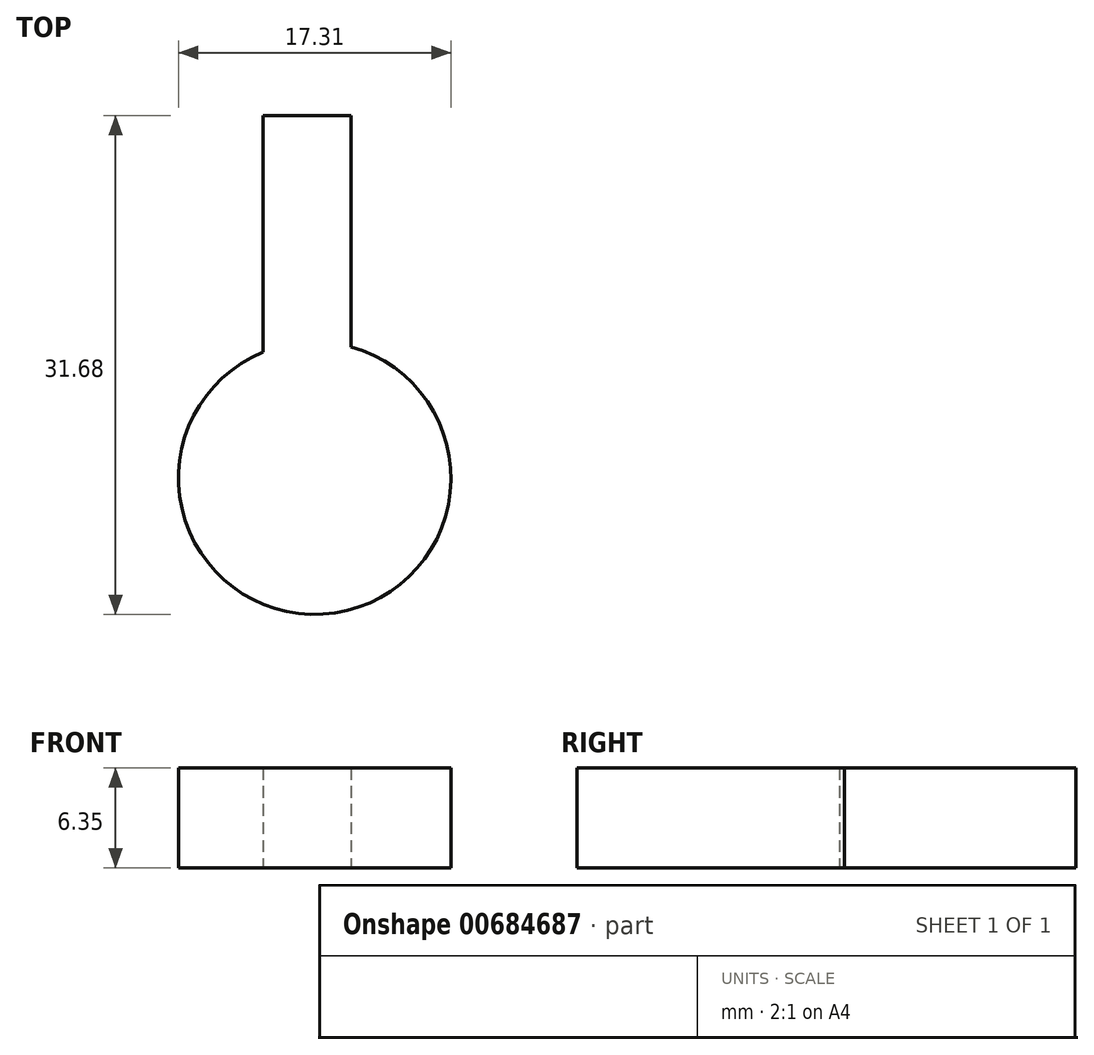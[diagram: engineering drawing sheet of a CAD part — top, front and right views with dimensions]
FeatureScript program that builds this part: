
annotation { "Feature Type Name" : "Feature", "Feature Type Description" : "" }
export const myFeature = defineFeature(function(context is Context, id is Id, definition is map)
    precondition{}
    {
        {
            var Q0;
            Q0=qCreatedBy(makeId("Top.planeOp"),FACE);
            var sketch = newSketch(context, id + "F0", { "sketchPlane" : qUnion([Q0])});
            skCircle(sketch, "E0", {"center": v(-6.76, 21.15) * mm, "radius": 8.65 * mm});
            skLineSegment(sketch, "E1.bottom", {"start": v(-10.05, 29.16) * mm, "end": v(-4.46, 29.16) * mm});
            skLineSegment(sketch, "E1.top", {"start": v(-10.05, 44.18) * mm, "end": v(-4.46, 44.18) * mm});
            skLineSegment(sketch, "E1.left", {"start": v(-10.05, 29.16) * mm, "end": v(-10.05, 44.18) * mm});
            skLineSegment(sketch, "E1.right", {"start": v(-4.46, 29.16) * mm, "end": v(-4.46, 44.18) * mm});
            skSolve(sketch);
        }
        {
            var Q0;
            Q0=qSketchRegion(id+"F0",true);
            extrude(context, id + "F1", {"entities" : qUnion([Q0]), "depth" : 6.35 * mm, "offsetDistance" : 25.4 * mm});
        }
    });
